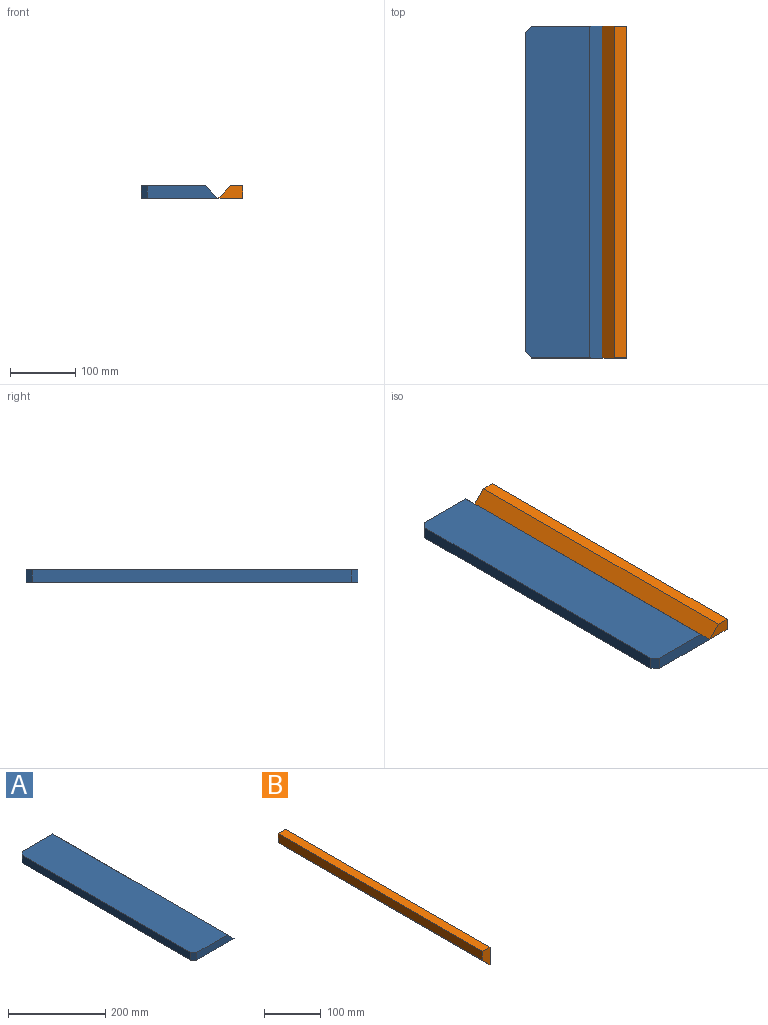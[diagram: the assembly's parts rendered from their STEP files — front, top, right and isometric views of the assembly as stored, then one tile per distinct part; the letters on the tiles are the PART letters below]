
ASSEMBLY  parts=2 mates=1
PART A: 8 faces, bbox 117.5x508x19.1 mm
  f0: plane 508x98.43mm, normal (0,0,1), area 49909.2mm2, adj f1,f3,f4,f5,f6,f7
  f1: plane 488.95x19.05mm, normal (-1,0,0), area 9314.5mm2, adj f0,f2,f6,f7
  f2: plane 508x117.48mm, normal (0,0,-1), area 59586.6mm2, adj f1,f3,f4,f5,f6,f7
  f3: plane 508x19.05mm, normal (0.71,0,0.71), area 13685.9mm2, adj f0,f2,f4,f5
  f4: plane 107.95x19.05mm, normal (0,-1,0), area 1875mm2, adj f0,f2,f3,f6
  f5: plane 107.95x19.05mm, normal (0,1,0), area 1875mm2, adj f0,f2,f3,f7
  f6: plane 19.05x9.53mm, normal (-0.71,-0.71,0), area 256.6mm2, adj f0,f1,f2,f4
  f7: plane 19.05x9.53mm, normal (-0.71,0.71,0), area 256.6mm2, adj f0,f1,f2,f5
PART B: 6 faces, bbox 19.1x508x38.1 mm
  f0: plane 508x38.1mm, normal (1,0,0), area 19354.8mm2, adj f1,f3,f4,f5
  f1: plane 508x19.05mm, normal (0,0,1), area 9677.4mm2, adj f0,f2,f4,f5
  f2: plane 508x19.05mm, normal (-1,0,0), area 9677.4mm2, adj f1,f3,f4,f5
  f3: plane 508x19.05mm, normal (-0.71,0,-0.71), area 13685.9mm2, adj f0,f2,f4,f5
  f4: plane 38.1x19.05mm, normal (0,-1,0), area 544.4mm2, adj f0,f1,f2,f3
  f5: plane 38.1x19.05mm, normal (0,1,0), area 544.4mm2, adj f0,f1,f2,f3
PLACE A at identity fixed
PLACE B rot(axis=(0,1,0),90deg) t=(107.95,0,146.05)mm
MATE fastened B.f4 <-> A.f4  axis (0,-1,0) through (127,-254,19.05)mm
